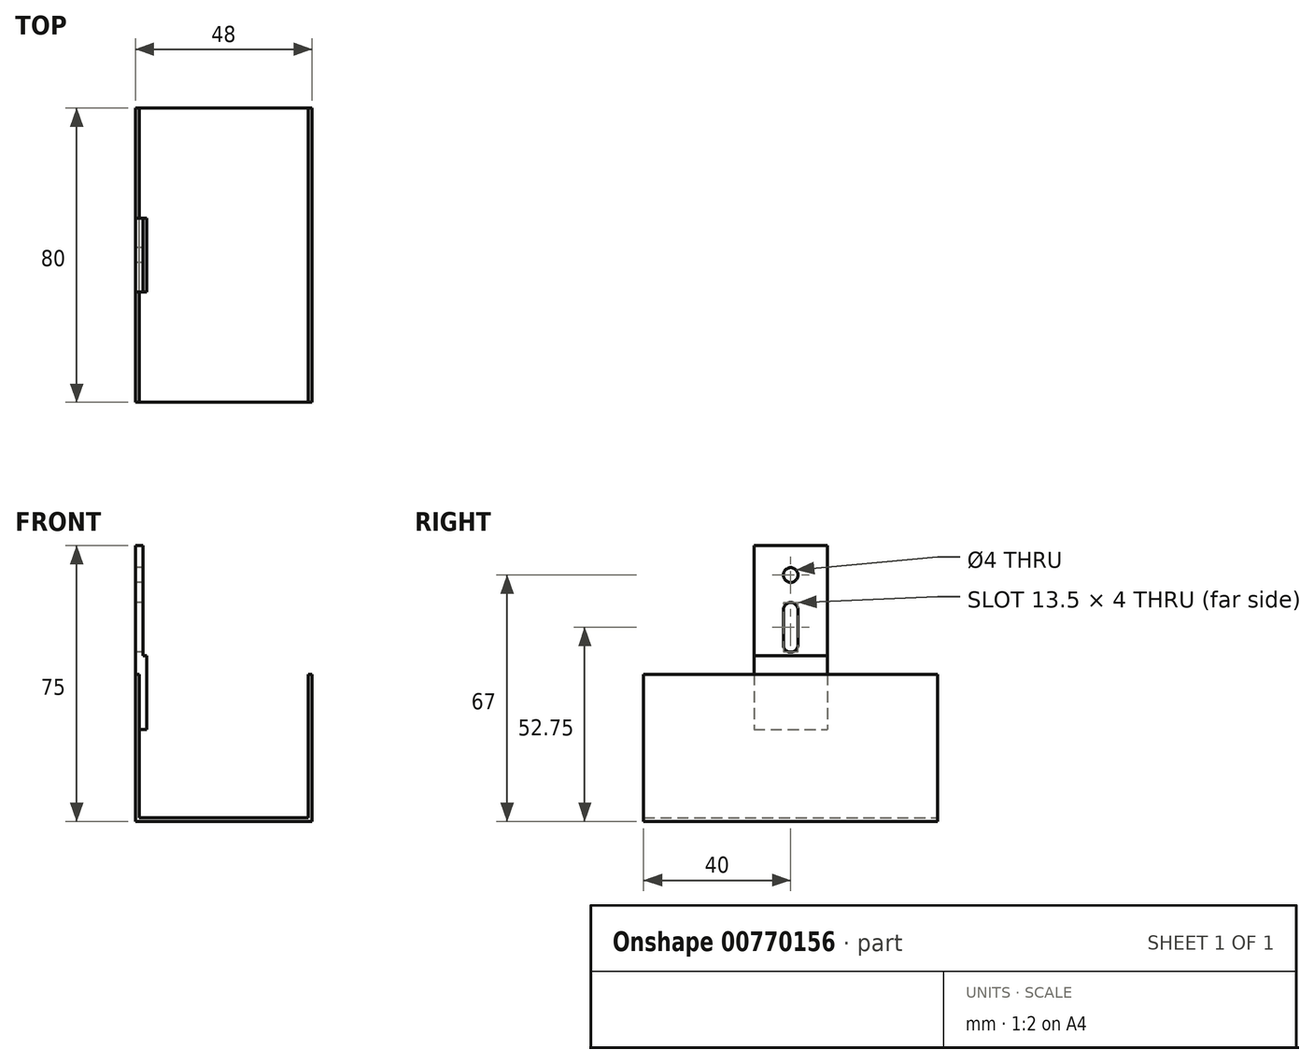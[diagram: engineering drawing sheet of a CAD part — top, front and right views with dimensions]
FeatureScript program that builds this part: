
annotation { "Feature Type Name" : "Feature", "Feature Type Description" : "" }
export const myFeature = defineFeature(function(context is Context, id is Id, definition is map)
    precondition{}
    {
        {
            var Q0;
            Q0=qCreatedBy(makeId("Front.planeOp"),FACE);
            var sketch = newSketch(context, id + "F0", { "sketchPlane" : qUnion([Q0])});
            skLineSegment(sketch, "E0.bottom", {"start": v(0, 0) * mm, "end": v(-24, 0) * mm});
            skLineSegment(sketch, "E0.right", {"start": v(-24, 0) * mm, "end": v(-24, 40) * mm});
            skLineSegment(sketch, "E1.bottom", {"start": v(0, 0) * mm, "end": v(-23, 0) * mm});
            skLineSegment(sketch, "E1.right", {"start": v(-23, 0) * mm, "end": v(-23, 40) * mm});
            skLineSegment(sketch, "E2.MirrorCS", {"start": v(24, 0) * mm, "end": v(24, 40) * mm});
            skLineSegment(sketch, "E3.MirrorCS", {"start": v(23, 0) * mm, "end": v(23, 40) * mm});
            skLineSegment(sketch, "E4.MirrorCS", {"start": v(0, 0) * mm, "end": v(23, 0) * mm});
            skLineSegment(sketch, "E5", {"start": v(-24, 1) * mm, "end": v(24, 1) * mm});
            skLineSegment(sketch, "E6", {"start": v(-24, 40) * mm, "end": v(-23, 40) * mm});
            skLineSegment(sketch, "E7", {"start": v(24, 40) * mm, "end": v(23, 40) * mm});
            skLineSegment(sketch, "E8", {"start": v(24, 0) * mm, "end": v(23, 0) * mm});
            skSolve(sketch);
        }
        {
            var Q0;
            Q0 = qSketchRegion(id + "F0", true);
            extrude(context, id + "F1", {"entities" : qUnion([Q0]), "depth" : 40 * mm, "offsetDistance" : 25 * mm, "hasSecondDirection" : true, "secondDirectionOppositeDirection" : true, "secondDirectionDepth" : 40 * mm});
        }
        {
            var Q0;
            Q0=qCreatedBy(makeId("Front.planeOp"),FACE);
            var sketch = newSketch(context, id + "F2", { "sketchPlane" : qUnion([Q0])});
            skLineSegment(sketch, "E9.0.0", {"start": v(-24, 40) * mm, "end": v(-24, 0) * mm, "construction": true});
            skLineSegment(sketch, "E9.0.1", {"start": v(-24, 0) * mm, "end": v(24, 0) * mm, "construction": true});
            skLineSegment(sketch, "E9.0.2", {"start": v(24, 0) * mm, "end": v(24, 40) * mm, "construction": true});
            skLineSegment(sketch, "E9.0.3", {"start": v(24, 40) * mm, "end": v(23, 40) * mm, "construction": true});
            skLineSegment(sketch, "E9.0.4", {"start": v(23, 40) * mm, "end": v(23, 1) * mm, "construction": true});
            skLineSegment(sketch, "E9.0.5", {"start": v(23, 1) * mm, "end": v(-23, 1) * mm, "construction": true});
            skLineSegment(sketch, "E9.0.6", {"start": v(-23, 1) * mm, "end": v(-23, 40) * mm, "construction": true});
            skLineSegment(sketch, "E9.0.7", {"start": v(-23, 40) * mm, "end": v(-24, 40) * mm, "construction": true});
            skLineSegment(sketch, "E10.bottom", {"start": v(-23, 40) * mm, "end": v(-21, 40) * mm});
            skLineSegment(sketch, "E10.top", {"start": v(-23, 25) * mm, "end": v(-21, 25) * mm});
            skLineSegment(sketch, "E10.left", {"start": v(-23, 40) * mm, "end": v(-23, 25) * mm});
            skLineSegment(sketch, "E10.right", {"start": v(-21, 40) * mm, "end": v(-21, 25) * mm});
            skLineSegment(sketch, "E11.bottom", {"start": v(-24, 40) * mm, "end": v(-21, 40) * mm});
            skLineSegment(sketch, "E11.top", {"start": v(-24, 45) * mm, "end": v(-21, 45) * mm});
            skLineSegment(sketch, "E11.left", {"start": v(-24, 40) * mm, "end": v(-24, 45) * mm});
            skLineSegment(sketch, "E11.right", {"start": v(-21, 40) * mm, "end": v(-21, 45) * mm});
            skPoint(sketch, "E12.oppositeSnap0", {"position": v(-22, 40) * mm});
            skLineSegment(sketch, "E12.bottom", {"start": v(-24, 45) * mm, "end": v(-22, 45) * mm});
            skLineSegment(sketch, "E12.top", {"start": v(-24, 75) * mm, "end": v(-22, 75) * mm});
            skLineSegment(sketch, "E12.left", {"start": v(-24, 45) * mm, "end": v(-24, 75) * mm});
            skLineSegment(sketch, "E12.right", {"start": v(-22, 45) * mm, "end": v(-22, 75) * mm});
            skSolve(sketch);
        }
        {
            var Q0;
            Q0 = qSketchRegion(id + "F2", true);
            extrude(context, id + "F3", {"entities" : qUnion([Q0]), "depth" : 10 * mm, "offsetDistance" : 25 * mm, "hasSecondDirection" : true, "secondDirectionOppositeDirection" : true, "secondDirectionDepth" : 10 * mm});
        }
        {
            var Q0;
            Q0=makeQuery(id+"F3.opExtrude","SWEPT_FACE",FACE,{"disambiguationData":[OSD([sQuery(id+"F2.wireOp",EDGE,"E11.left"),sQuery(id+"F2.wireOp",EDGE,"E12.left")])]});
            var sketch = newSketch(context, id + "F4", { "sketchPlane" : qUnion([Q0])});
            skLineSegment(sketch, "E13.0.0", {"start": v(-10, 75) * mm, "end": v(-10, 40) * mm, "construction": true});
            skLineSegment(sketch, "E13.0.1", {"start": v(-10, 40) * mm, "end": v(10, 40) * mm, "construction": true});
            skLineSegment(sketch, "E13.0.2", {"start": v(10, 40) * mm, "end": v(10, 75) * mm, "construction": true});
            skLineSegment(sketch, "E13.0.3", {"start": v(10, 75) * mm, "end": v(-10, 75) * mm, "construction": true});
            skPoint(sketch, "E14", {"position": v(0, 57.5) * mm});
            skPoint(sketch, "E14.positionSnap0", {"position": v(-10, 57.5) * mm});
            skPoint(sketch, "E14.positionSnap1", {"position": v(0, 75) * mm});
            skPoint(sketch, "E15", {"position": v(0, 67) * mm});
            skCircle(sketch, "E16", {"center": v(0, 67) * mm, "radius": 2 * mm});
            skArc(sketch, "E17", {"start": v(2, 57.5) * mm, "mid": v(0, 59.5) * mm, "end": v(-2, 57.5) * mm});
            skLineSegment(sketch, "E18", {"start": v(0, 57.5) * mm, "end": v(-10, 57.5) * mm, "construction": true});
            skArc(sketch, "E19.MirrorC", {"start": v(2, 48) * mm, "mid": v(0, 46) * mm, "end": v(-2, 48) * mm});
            skLineSegment(sketch, "E20", {"start": v(2, 48) * mm, "end": v(2, 57.5) * mm});
            skLineSegment(sketch, "E21", {"start": v(-2, 57.5) * mm, "end": v(-2, 48) * mm});
            skSolve(sketch);
        }
        {
            var Q0;
            Q0 = qSketchRegion(id + "F4", true);
            extrude(context, id + "F5", {"entities" : qUnion([Q0]), "operationType" : NewBodyOperationType.REMOVE, "oppositeDirection" : true, "depth" : 10 * mm, "offsetDistance" : 25 * mm});
        }
    });
